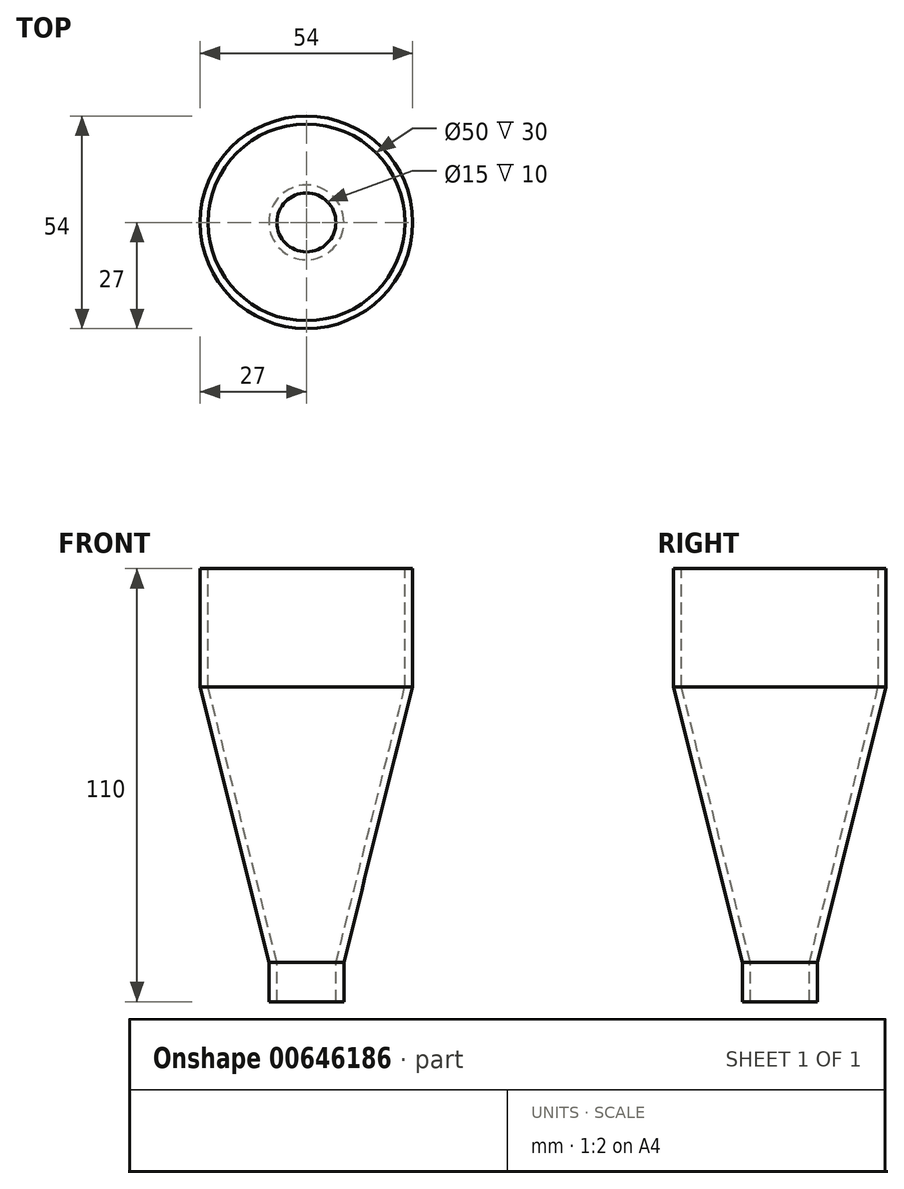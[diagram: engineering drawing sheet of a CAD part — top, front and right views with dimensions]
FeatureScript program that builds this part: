
annotation { "Feature Type Name" : "Feature", "Feature Type Description" : "" }
export const myFeature = defineFeature(function(context is Context, id is Id, definition is map)
    precondition{}
    {
        {
            var Q0;
            Q0=qCreatedBy(makeId("Front.planeOp"),FACE);
            var sketch = newSketch(context, id + "F0", { "sketchPlane" : qUnion([Q0])});
            skLineSegment(sketch, "E0", {"start": v(0, 63.29) * mm, "end": v(0, -63.29) * mm, "construction": true});
            skLineSegment(sketch, "E1", {"start": v(-25, 0) * mm, "end": v(-25, -30) * mm});
            skLineSegment(sketch, "E2", {"start": v(-25, -30) * mm, "end": v(-7.5, -100) * mm});
            skLineSegment(sketch, "E3", {"start": v(-7.5, -100) * mm, "end": v(-7.5, -110) * mm});
            skLineSegment(sketch, "E4", {"start": v(-7.5, -110) * mm, "end": v(-9.5, -110) * mm});
            skLineSegment(sketch, "E5", {"start": v(-9.5, -110) * mm, "end": v(-9.5, -100) * mm});
            skLineSegment(sketch, "E6", {"start": v(-9.5, -100) * mm, "end": v(-27, -30) * mm});
            skLineSegment(sketch, "E7", {"start": v(-27, -30) * mm, "end": v(-27, 0) * mm});
            skLineSegment(sketch, "E8", {"start": v(-27, 0) * mm, "end": v(-25, 0) * mm});
            skSolve(sketch);
        }
        {
            var Q0;
            Q0 = qSketchRegion(id + "F0", true);
            var Q1;
            Q1=sQuery(id+"F0.wireOp",EDGE,"E0");
            revolve(context, id + "F1", {"entities" : qUnion([Q0]), "axis" : qUnion([Q1]), "revolveType" : RevolveType.FULL});
        }
    });
